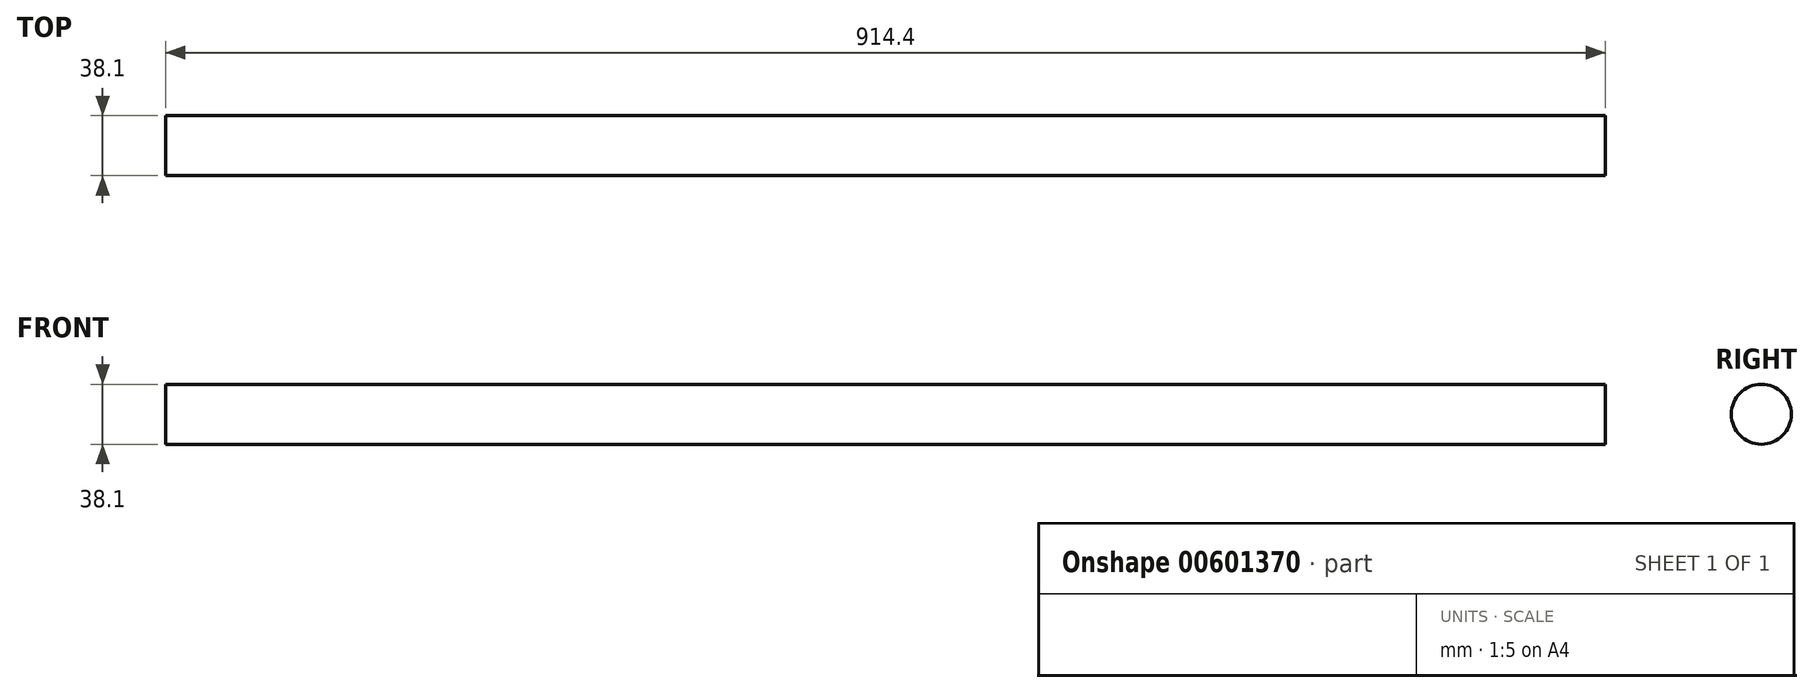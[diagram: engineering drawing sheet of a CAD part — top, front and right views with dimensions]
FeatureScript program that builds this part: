
annotation { "Feature Type Name" : "Feature", "Feature Type Description" : "" }
export const myFeature = defineFeature(function(context is Context, id is Id, definition is map)
    precondition{}
    {
        {
            var Q0;
            Q0=qCreatedBy(makeId("Front.planeOp"),FACE);
            var sketch = newSketch(context, id + "F0", { "sketchPlane" : qUnion([Q0])});
            skLineSegment(sketch, "E0", {"start": v(0, -213.29) * mm, "end": v(-457.2, -213.29) * mm});
            skLineSegment(sketch, "E1", {"start": v(0, 917.01) * mm, "end": v(0, -328.98) * mm, "construction": true});
            skLineSegment(sketch, "E2", {"start": v(-457.2, -213.29) * mm, "end": v(-457.2, -194.24) * mm});
            skLineSegment(sketch, "E3", {"start": v(-457.2, -175.19) * mm, "end": v(-457.2, -175.19) * mm});
            skLineSegment(sketch, "E4.MirrorCS", {"start": v(457.2, -213.29) * mm, "end": v(457.2, -213.29) * mm});
            skLineSegment(sketch, "E5.MirrorCS", {"start": v(0, -213.29) * mm, "end": v(457.2, -213.29) * mm});
            skLineSegment(sketch, "E6.MirrorCS", {"start": v(457.2, -175.19) * mm, "end": v(0, -175.19) * mm});
            skLineSegment(sketch, "E7", {"start": v(-457.2, -194.24) * mm, "end": v(457.2, -194.24) * mm});
            skLineSegment(sketch, "E8", {"start": v(-457.2, -194.24) * mm, "end": v(-457.2, -194.24) * mm});
            skLineSegment(sketch, "E9", {"start": v(457.2, -194.24) * mm, "end": v(457.2, -175.19) * mm});
            skLineSegment(sketch, "E10", {"start": v(457.2, -175.19) * mm, "end": v(457.2, -175.19) * mm});
            skLineSegment(sketch, "E11", {"start": v(457.2, -194.24) * mm, "end": v(457.2, -194.24) * mm});
            skLineSegment(sketch, "E12", {"start": v(-457.2, -213.29) * mm, "end": v(-457.2, -213.29) * mm});
            skLineSegment(sketch, "E13", {"start": v(-457.2, -194.24) * mm, "end": v(-457.2, -175.19) * mm});
            skLineSegment(sketch, "E14", {"start": v(-457.2, -175.19) * mm, "end": v(0, -175.19) * mm});
            skLineSegment(sketch, "E15", {"start": v(457.2, -213.29) * mm, "end": v(457.2, -194.24) * mm});
            skLineSegment(sketch, "E16", {"start": v(-457.2, 917.01) * mm, "end": v(-457.2, 917.01) * mm});
            skLineSegment(sketch, "E17", {"start": v(-457.2, 917.01) * mm, "end": v(-457.2, 955.11) * mm});
            skLineSegment(sketch, "E18", {"start": v(-457.2, 955.11) * mm, "end": v(-457.2, 955.11) * mm});
            skLineSegment(sketch, "E19", {"start": v(457.2, 955.11) * mm, "end": v(457.2, 917.01) * mm});
            skLineSegment(sketch, "E20", {"start": v(-457.2, 936.06) * mm, "end": v(457.2, 936.06) * mm});
            skLineSegment(sketch, "E21", {"start": v(-457.2, 955.11) * mm, "end": v(457.2, 955.11) * mm});
            skLineSegment(sketch, "E22", {"start": v(-457.2, 917.01) * mm, "end": v(457.2, 917.01) * mm});
            skSolve(sketch);
        }
        {
            var Q0;
            {var subQ2=sQuery(id+"F0.wireOp",EDGE,"E20");Q0=makeQuery(id+"F0.imprint","IMPRINT",FACE,{"disambiguationData":[TD([[makeQuery(id+"F0.imprint","IMPRINT",EDGE,{"derivedFrom":subQ2}),-1.0]])]});}
            var Q1;
            Q1=sQuery(id+"F0.wireOp",EDGE,"E21");
            var Q2;
            Q2=sQuery(id+"F0.wireOp",EDGE,"E20");
            revolve(context, id + "F1", {"bodyType" : ToolBodyType.SURFACE, "operationType" : NewBodyOperationType.ADD, "entities" : qUnion([Q0]), "surfaceEntities" : qUnion([Q1]), "axis" : qUnion([Q2]), "revolveType" : RevolveType.ONE_DIRECTION, "angle" : 360 * degree});
        }
        {
            var Q0;
            Q0=makeQuery(id+"F0.imprint","IMPRINT",FACE,{"disambiguationData":[TD([[makeQuery(id+"F0.imprint","IMPRINT",EDGE,{"derivedFrom":sQuery(id+"F0.wireOp",EDGE,"E6.MirrorCS")}),1.0]])]});
            var Q1;
            Q1=sQuery(id+"F0.wireOp",EDGE,"E7");
            revolve(context, id + "F2", {"entities" : qUnion([Q0]), "axis" : qUnion([Q1]), "revolveType" : RevolveType.FULL});
        }
    });
